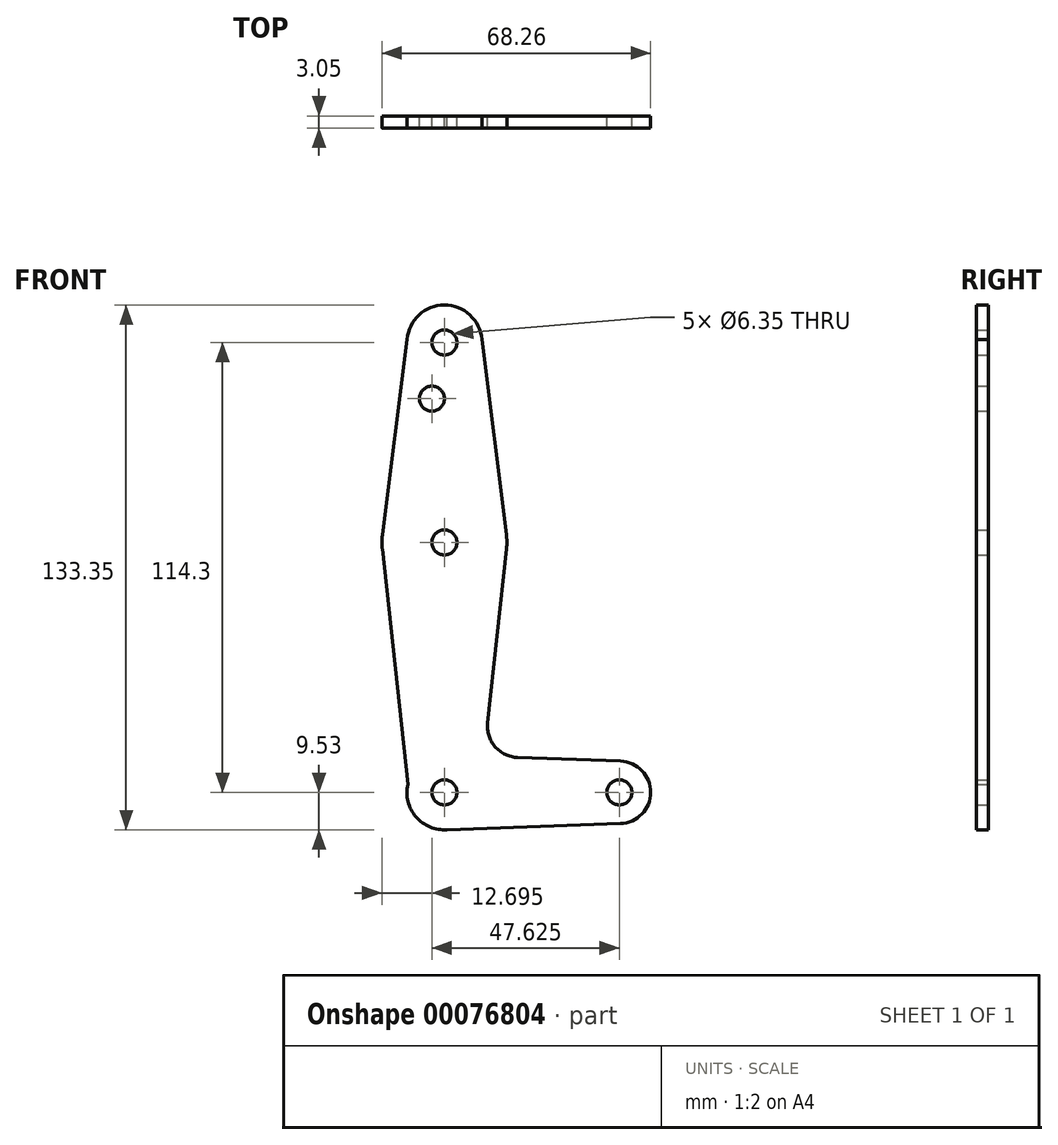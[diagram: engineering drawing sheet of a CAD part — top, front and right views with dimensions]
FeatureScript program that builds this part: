
annotation { "Feature Type Name" : "Feature", "Feature Type Description" : "" }
export const myFeature = defineFeature(function(context is Context, id is Id, definition is map)
    precondition{}
    {
        {
            var Q0;
            Q0=qCreatedBy(makeId("Front.planeOp"),FACE);
            var sketch = newSketch(context, id + "F0", { "sketchPlane" : qUnion([Q0])});
            skLineSegment(sketch, "E0", {"start": v(0, 0) * mm, "end": v(0, 114.3) * mm, "construction": true});
            skLineSegment(sketch, "E1", {"start": v(0, 0) * mm, "end": v(44.45, 0) * mm, "construction": true});
            skCircle(sketch, "E2", {"center": v(0, 114.3) * mm, "radius": 9.53 * mm});
            skCircle(sketch, "E3", {"center": v(0, 63.5) * mm, "radius": 15.88 * mm});
            skCircle(sketch, "E4", {"center": v(0, 0) * mm, "radius": 9.53 * mm});
            skCircle(sketch, "E5", {"center": v(44.45, 0) * mm, "radius": 7.94 * mm});
            skLineSegment(sketch, "E6", {"start": v(-9.4, 115.89) * mm, "end": v(-15.75, 65.49) * mm});
            skLineSegment(sketch, "E7", {"start": v(9.4, 115.89) * mm, "end": v(15.75, 65.49) * mm});
            skLineSegment(sketch, "E8", {"start": v(-9.3, 2.04) * mm, "end": v(-15.78, 61.79) * mm});
            skLineSegment(sketch, "E9", {"start": v(15.78, 61.79) * mm, "end": v(11, 17.66) * mm});
            skLineSegment(sketch, "E10", {"start": v(18.62, 8.86) * mm, "end": v(44.73, 7.93) * mm});
            skLineSegment(sketch, "E11", {"start": v(0, -9.53) * mm, "end": v(44.73, -7.93) * mm});
            skCircle(sketch, "E12", {"center": v(0, 114.3) * mm, "radius": 3.18 * mm});
            skCircle(sketch, "E13", {"center": v(0, 0) * mm, "radius": 3.18 * mm});
            skCircle(sketch, "E14", {"center": v(44.45, 0) * mm, "radius": 3.18 * mm});
            skCircle(sketch, "E15", {"center": v(0, 63.5) * mm, "radius": 3.18 * mm});
            skArc(sketch, "E16.filletArc", {"start": v(11, 17.66) * mm, "mid": v(12.9, 11.6) * mm, "end": v(18.62, 8.86) * mm});
            skCircle(sketch, "E17", {"center": v(-3.18, 100.03) * mm, "radius": 3.18 * mm});
            skSolve(sketch);
        }
        {
            var Q0;
            Q0 = qSketchRegion(id + "F0", true);
            extrude(context, id + "F1", {"entities" : qUnion([Q0]), "depth" : 3.05 * mm});
        }
    });
